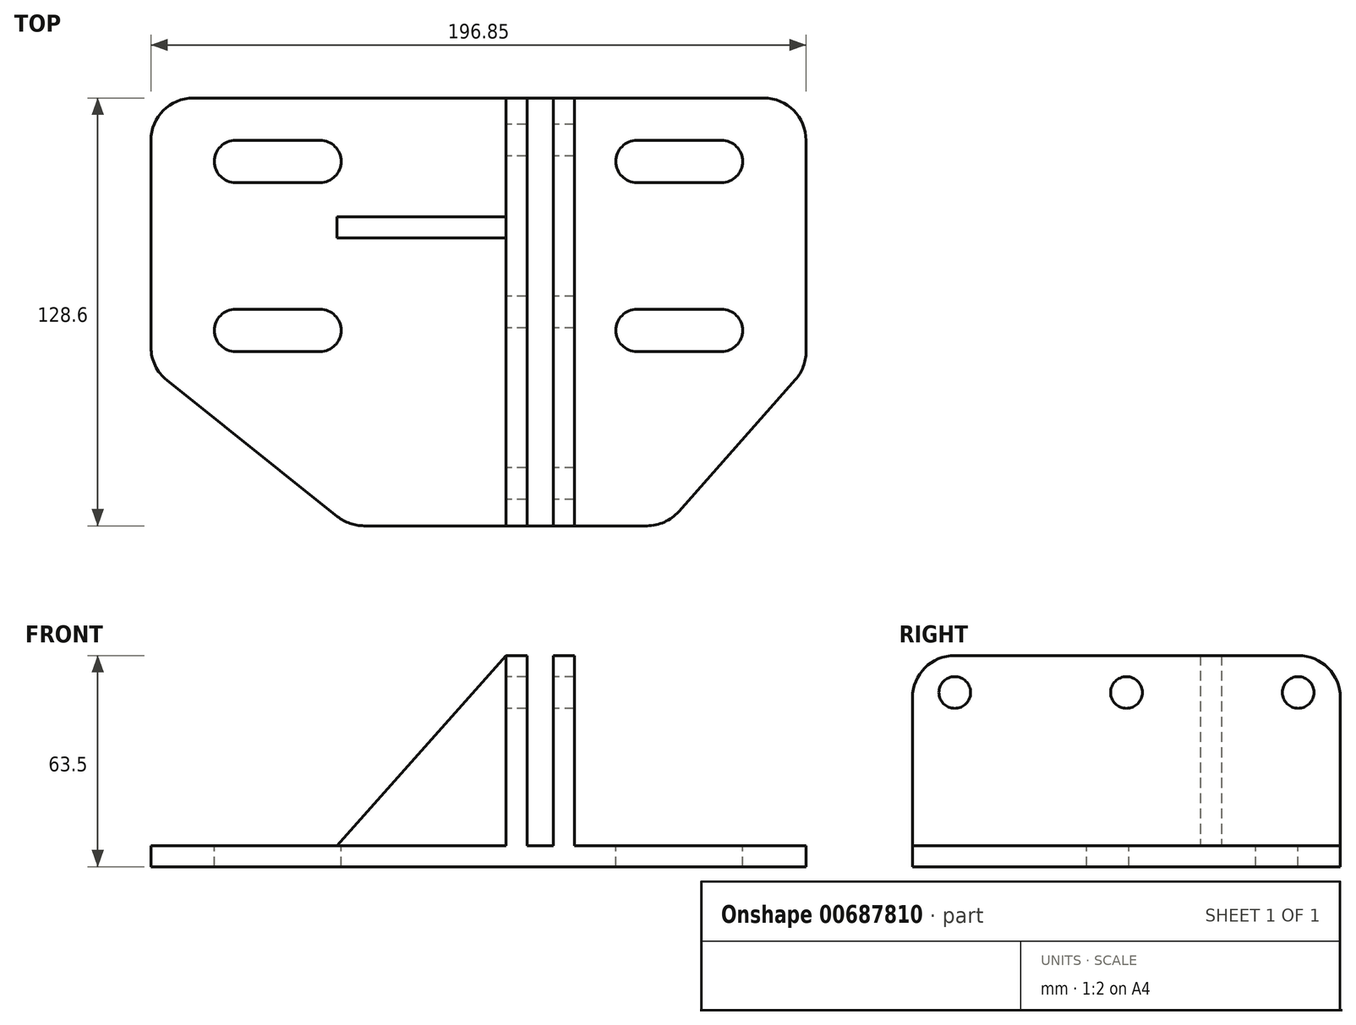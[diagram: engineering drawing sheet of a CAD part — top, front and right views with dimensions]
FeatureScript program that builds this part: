
annotation { "Feature Type Name" : "Feature", "Feature Type Description" : "" }
export const myFeature = defineFeature(function(context is Context, id is Id, definition is map)
    precondition{}
    {
        {
            var Q0;
            Q0=qCreatedBy(makeId("Top.planeOp"),FACE);
            var sketch = newSketch(context, id + "F0", { "sketchPlane" : qUnion([Q0])});
            skLineSegment(sketch, "E0", {"start": v(-88.28, 54.8) * mm, "end": v(83.17, 54.8) * mm});
            skLineSegment(sketch, "E1", {"start": v(95.87, 42.1) * mm, "end": v(95.87, -21.42) * mm});
            skLineSegment(sketch, "E2", {"start": v(92.69, -29.84) * mm, "end": v(57.6, -69.51) * mm});
            skLineSegment(sketch, "E3", {"start": v(48.08, -73.8) * mm, "end": v(-37, -73.8) * mm});
            skLineSegment(sketch, "E4", {"start": v(-44.92, -71.02) * mm, "end": v(-96.2, -30.05) * mm});
            skLineSegment(sketch, "E5", {"start": v(-100.98, -20.13) * mm, "end": v(-100.98, 42.1) * mm});
            skPoint(sketch, "E6.visualSharp", {"position": v(-100.98, 54.8) * mm});
            skArc(sketch, "E6.filletArc", {"start": v(-88.28, 54.8) * mm, "mid": v(-97.26, 51.08) * mm, "end": v(-100.98, 42.1) * mm});
            skPoint(sketch, "E7.visualSharp", {"position": v(95.87, 54.8) * mm});
            skArc(sketch, "E7.filletArc", {"start": v(95.87, 42.1) * mm, "mid": v(92.15, 51.08) * mm, "end": v(83.17, 54.8) * mm});
            skPoint(sketch, "E8.visualSharp", {"position": v(-41.45, -73.8) * mm});
            skArc(sketch, "E8.filletArc", {"start": v(-44.92, -71.02) * mm, "mid": v(-41.2, -73.09) * mm, "end": v(-37, -73.8) * mm});
            skPoint(sketch, "E9.visualSharp", {"position": v(53.8, -73.8) * mm});
            skArc(sketch, "E9.filletArc", {"start": v(48.08, -73.8) * mm, "mid": v(53.3, -72.68) * mm, "end": v(57.6, -69.51) * mm});
            skPoint(sketch, "E10.visualSharp", {"position": v(-100.98, -26.23) * mm});
            skArc(sketch, "E10.filletArc", {"start": v(-100.98, -20.13) * mm, "mid": v(-99.72, -25.63) * mm, "end": v(-96.2, -30.05) * mm});
            skPoint(sketch, "E11.visualSharp", {"position": v(95.87, -26.23) * mm});
            skArc(sketch, "E11.filletArc", {"start": v(92.69, -29.84) * mm, "mid": v(95.05, -25.92) * mm, "end": v(95.87, -21.42) * mm});
            skSolve(sketch);
        }
        {
            var Q0;
            Q0=makeQuery(id+"F0.imprint","IMPRINT",FACE,{"disambiguationData":[TD([[makeQuery(id+"F0.imprint","IMPRINT",EDGE,{"derivedFrom":sQuery(id+"F0.wireOp",EDGE,"E0")}),-1.0]])]});
            extrude(context, id + "F1", {"entities" : qUnion([Q0]), "depth" : 6.35 * mm, "offsetDistance" : 25.4 * mm});
        }
        {
            var Q0;
            Q0=makeQuery(id+"F1.opExtrude","CAP_FACE",FACE,{"disambiguationData":[OSD([sQuery(id+"F0.wireOp",EDGE,"E0"),sQuery(id+"F0.wireOp",EDGE,"E1"),sQuery(id+"F0.wireOp",EDGE,"E2"),sQuery(id+"F0.wireOp",EDGE,"E3"),sQuery(id+"F0.wireOp",EDGE,"E4"),sQuery(id+"F0.wireOp",EDGE,"E5"),sQuery(id+"F0.wireOp",EDGE,"E6.filletArc"),sQuery(id+"F0.wireOp",EDGE,"E7.filletArc"),sQuery(id+"F0.wireOp",EDGE,"E8.filletArc"),sQuery(id+"F0.wireOp",EDGE,"E9.filletArc"),sQuery(id+"F0.wireOp",EDGE,"E10.filletArc"),sQuery(id+"F0.wireOp",EDGE,"E11.filletArc")])],"isStart":false});
            var sketch = newSketch(context, id + "F2", { "sketchPlane" : qUnion([Q0])});
            skLineSegment(sketch, "E12.bottom", {"start": v(-50.18, -8.7) * mm, "end": v(-75.58, -8.7) * mm});
            skLineSegment(sketch, "E12.top", {"start": v(-50.18, -21.4) * mm, "end": v(-75.58, -21.4) * mm});
            skLineSegment(sketch, "E12.left", {"start": v(-43.83, -15.05) * mm, "end": v(-43.83, -15.05) * mm});
            skLineSegment(sketch, "E12.right", {"start": v(-81.93, -15.05) * mm, "end": v(-81.93, -15.05) * mm});
            skPoint(sketch, "E12.middle", {"position": v(-62.88, -15.05) * mm});
            skLineSegment(sketch, "E13.bottom", {"start": v(70.47, -8.7) * mm, "end": v(45.07, -8.7) * mm});
            skLineSegment(sketch, "E13.top", {"start": v(70.47, -21.4) * mm, "end": v(45.07, -21.4) * mm});
            skLineSegment(sketch, "E13.left", {"start": v(76.82, -15.05) * mm, "end": v(76.82, -15.05) * mm});
            skLineSegment(sketch, "E13.right", {"start": v(38.72, -15.05) * mm, "end": v(38.72, -15.05) * mm});
            skPoint(sketch, "E13.middle", {"position": v(57.77, -15.05) * mm});
            skLineSegment(sketch, "E14.bottom", {"start": v(45.07, 42.1) * mm, "end": v(70.47, 42.1) * mm});
            skLineSegment(sketch, "E14.top", {"start": v(45.07, 29.4) * mm, "end": v(70.47, 29.4) * mm});
            skLineSegment(sketch, "E14.left", {"start": v(38.72, 35.75) * mm, "end": v(38.72, 35.75) * mm});
            skLineSegment(sketch, "E14.right", {"start": v(76.82, 35.75) * mm, "end": v(76.82, 35.75) * mm});
            skPoint(sketch, "E14.middle", {"position": v(57.77, 35.75) * mm});
            skLineSegment(sketch, "E15.bottom", {"start": v(-75.58, 42.1) * mm, "end": v(-50.18, 42.1) * mm});
            skLineSegment(sketch, "E15.top", {"start": v(-75.58, 29.4) * mm, "end": v(-50.18, 29.4) * mm});
            skLineSegment(sketch, "E15.left", {"start": v(-81.93, 35.75) * mm, "end": v(-81.93, 35.75) * mm});
            skLineSegment(sketch, "E15.right", {"start": v(-43.83, 35.75) * mm, "end": v(-43.83, 35.75) * mm});
            skPoint(sketch, "E15.middle", {"position": v(-62.88, 35.75) * mm});
            skPoint(sketch, "E16.visualSharp", {"position": v(-81.93, -21.4) * mm});
            skArc(sketch, "E16.filletArc", {"start": v(-81.93, -15.05) * mm, "mid": v(-80.07, -19.54) * mm, "end": v(-75.58, -21.4) * mm});
            skPoint(sketch, "E17.visualSharp", {"position": v(-81.93, -8.7) * mm});
            skArc(sketch, "E17.filletArc", {"start": v(-75.58, -8.7) * mm, "mid": v(-80.07, -10.56) * mm, "end": v(-81.93, -15.05) * mm});
            skPoint(sketch, "E18.visualSharp", {"position": v(-43.83, -21.4) * mm});
            skArc(sketch, "E18.filletArc", {"start": v(-50.18, -21.4) * mm, "mid": v(-45.69, -19.54) * mm, "end": v(-43.83, -15.05) * mm});
            skPoint(sketch, "E19.visualSharp", {"position": v(-43.83, -8.7) * mm});
            skArc(sketch, "E19.filletArc", {"start": v(-43.83, -15.05) * mm, "mid": v(-45.69, -10.56) * mm, "end": v(-50.18, -8.7) * mm});
            skPoint(sketch, "E20.visualSharp", {"position": v(-43.83, 29.4) * mm});
            skArc(sketch, "E20.filletArc", {"start": v(-50.18, 29.4) * mm, "mid": v(-45.69, 31.26) * mm, "end": v(-43.83, 35.75) * mm});
            skPoint(sketch, "E21.visualSharp", {"position": v(-43.83, 42.1) * mm});
            skArc(sketch, "E21.filletArc", {"start": v(-43.83, 35.75) * mm, "mid": v(-45.69, 40.24) * mm, "end": v(-50.18, 42.1) * mm});
            skPoint(sketch, "E22.visualSharp", {"position": v(-81.93, 42.1) * mm});
            skArc(sketch, "E22.filletArc", {"start": v(-75.58, 42.1) * mm, "mid": v(-80.07, 40.24) * mm, "end": v(-81.93, 35.75) * mm});
            skPoint(sketch, "E23.visualSharp", {"position": v(-81.93, 29.4) * mm});
            skArc(sketch, "E23.filletArc", {"start": v(-81.93, 35.75) * mm, "mid": v(-80.07, 31.26) * mm, "end": v(-75.58, 29.4) * mm});
            skPoint(sketch, "E24.visualSharp", {"position": v(38.72, -21.4) * mm});
            skArc(sketch, "E24.filletArc", {"start": v(38.72, -15.05) * mm, "mid": v(40.58, -19.54) * mm, "end": v(45.07, -21.4) * mm});
            skPoint(sketch, "E25.visualSharp", {"position": v(38.72, -8.7) * mm});
            skArc(sketch, "E25.filletArc", {"start": v(45.07, -8.7) * mm, "mid": v(40.58, -10.56) * mm, "end": v(38.72, -15.05) * mm});
            skPoint(sketch, "E26.visualSharp", {"position": v(76.82, -21.4) * mm});
            skArc(sketch, "E26.filletArc", {"start": v(70.47, -21.4) * mm, "mid": v(74.96, -19.54) * mm, "end": v(76.82, -15.05) * mm});
            skPoint(sketch, "E27.visualSharp", {"position": v(76.82, -8.7) * mm});
            skArc(sketch, "E27.filletArc", {"start": v(76.82, -15.05) * mm, "mid": v(74.96, -10.56) * mm, "end": v(70.47, -8.7) * mm});
            skPoint(sketch, "E28.visualSharp", {"position": v(76.82, 29.4) * mm});
            skArc(sketch, "E28.filletArc", {"start": v(70.47, 29.4) * mm, "mid": v(74.96, 31.26) * mm, "end": v(76.82, 35.75) * mm});
            skPoint(sketch, "E29.visualSharp", {"position": v(76.82, 42.1) * mm});
            skArc(sketch, "E29.filletArc", {"start": v(76.82, 35.75) * mm, "mid": v(74.96, 40.24) * mm, "end": v(70.47, 42.1) * mm});
            skPoint(sketch, "E30.visualSharp", {"position": v(38.72, 42.1) * mm});
            skArc(sketch, "E30.filletArc", {"start": v(45.07, 42.1) * mm, "mid": v(40.58, 40.24) * mm, "end": v(38.72, 35.75) * mm});
            skPoint(sketch, "E31.visualSharp", {"position": v(38.72, 29.4) * mm});
            skArc(sketch, "E31.filletArc", {"start": v(38.72, 35.75) * mm, "mid": v(40.58, 31.26) * mm, "end": v(45.07, 29.4) * mm});
            skSolve(sketch);
        }
        {
            var Q0;
            Q0 = qSketchRegion(id + "F2", true);
            extrude(context, id + "F3", {"entities" : qUnion([Q0]), "operationType" : NewBodyOperationType.REMOVE, "endBound" : BoundingType.THROUGH_ALL, "oppositeDirection" : true, "depth" : 25.4 * mm, "offsetDistance" : 25.4 * mm});
        }
        {
            var Q0;
            Q0=makeQuery(id+"F1.opExtrude","CAP_FACE",FACE,{"disambiguationData":[OSD([sQuery(id+"F0.wireOp",EDGE,"E0"),sQuery(id+"F0.wireOp",EDGE,"E1"),sQuery(id+"F0.wireOp",EDGE,"E2"),sQuery(id+"F0.wireOp",EDGE,"E3"),sQuery(id+"F0.wireOp",EDGE,"E4"),sQuery(id+"F0.wireOp",EDGE,"E5"),sQuery(id+"F0.wireOp",EDGE,"E6.filletArc"),sQuery(id+"F0.wireOp",EDGE,"E7.filletArc"),sQuery(id+"F0.wireOp",EDGE,"E8.filletArc"),sQuery(id+"F0.wireOp",EDGE,"E9.filletArc"),sQuery(id+"F0.wireOp",EDGE,"E10.filletArc"),sQuery(id+"F0.wireOp",EDGE,"E11.filletArc")])],"isStart":false});
            var sketch = newSketch(context, id + "F4", { "sketchPlane" : qUnion([Q0])});
            skLineSegment(sketch, "E32.bottom", {"start": v(5.7, 54.8) * mm, "end": v(12.04, 54.8) * mm});
            skLineSegment(sketch, "E32.top", {"start": v(5.7, -73.8) * mm, "end": v(12.04, -73.8) * mm});
            skLineSegment(sketch, "E32.left", {"start": v(5.7, 54.8) * mm, "end": v(5.7, -73.8) * mm});
            skLineSegment(sketch, "E32.right", {"start": v(12.04, 54.8) * mm, "end": v(12.04, -73.8) * mm});
            skLineSegment(sketch, "E33.bottom", {"start": v(26.33, 54.8) * mm, "end": v(19.98, 54.8) * mm});
            skLineSegment(sketch, "E33.top", {"start": v(26.33, -73.8) * mm, "end": v(19.98, -73.8) * mm});
            skLineSegment(sketch, "E33.left", {"start": v(26.33, 54.8) * mm, "end": v(26.33, -73.8) * mm});
            skLineSegment(sketch, "E33.right", {"start": v(19.98, 54.8) * mm, "end": v(19.98, -73.8) * mm});
            skSolve(sketch);
        }
        {
            var Q0;
            Q0 = qSketchRegion(id + "F4", true);
            extrude(context, id + "F5", {"entities" : qUnion([Q0]), "operationType" : NewBodyOperationType.ADD, "depth" : 57.15 * mm, "offsetDistance" : 25.4 * mm});
        }
        {
            var Q0;
            Q0=makeQuery(id+"F5.opExtrude","SWEPT_FACE",FACE,{"disambiguationData":[OSD([sQuery(id+"F4.wireOp",EDGE,"E32.left")])]});
            var sketch = newSketch(context, id + "F6", { "sketchPlane" : qUnion([Q0])});
            skCircle(sketch, "E34", {"center": v(-42.1, 52.39) * mm, "radius": 4.76 * mm});
            skCircle(sketch, "E35", {"center": v(9.5, 52.39) * mm, "radius": 4.76 * mm});
            skCircle(sketch, "E36", {"center": v(61.1, 52.39) * mm, "radius": 4.76 * mm});
            skSolve(sketch);
        }
        {
            var Q0;
            Q0=makeQuery(id+"F6.imprint","IMPRINT",FACE,{"disambiguationData":[TD([[makeQuery(id+"F6.imprint","IMPRINT",EDGE,{"derivedFrom":sQuery(id+"F6.wireOp",EDGE,"E34")}),1.0]])]});
            var Q1;
            Q1=makeQuery(id+"F6.imprint","IMPRINT",FACE,{"disambiguationData":[TD([[makeQuery(id+"F6.imprint","IMPRINT",EDGE,{"derivedFrom":sQuery(id+"F6.wireOp",EDGE,"E35")}),1.0]])]});
            var Q2;
            Q2=makeQuery(id+"F6.imprint","IMPRINT",FACE,{"disambiguationData":[TD([[makeQuery(id+"F6.imprint","IMPRINT",EDGE,{"derivedFrom":sQuery(id+"F6.wireOp",EDGE,"E36")}),1.0]])]});
            extrude(context, id + "F7", {"entities" : qUnion([Q0, Q1, Q2]), "operationType" : NewBodyOperationType.REMOVE, "endBound" : BoundingType.THROUGH_ALL, "oppositeDirection" : true, "depth" : 25.4 * mm, "offsetDistance" : 25.4 * mm});
        }
        {
            var Q0;
            Q0=qCreatedBy(makeId("Front.planeOp"),FACE);
            cPlane(context, id + "F8", {"entities" : qUnion([Q0]), "cplaneType" : CPlaneType.OFFSET, "offset" : 12.7 * mm, "oppositeDirection" : true, "width" : 152.4 * mm, "height" : 152.4 * mm});
        }
        {
            var Q0;
            Q0=qCreatedBy(id+"F8.planeOp",FACE);
            var sketch = newSketch(context, id + "F9", { "sketchPlane" : qUnion([Q0])});
            skLineSegment(sketch, "E37", {"start": v(5.7, 63.5) * mm, "end": v(5.7, 6.35) * mm});
            skLineSegment(sketch, "E38", {"start": v(5.7, 6.35) * mm, "end": v(-45.1, 6.35) * mm});
            skLineSegment(sketch, "E39", {"start": v(-45.1, 6.35) * mm, "end": v(5.7, 63.5) * mm});
            skSolve(sketch);
        }
        {
            var Q0;
            Q0 = qSketchRegion(id + "F9", true);
            extrude(context, id + "F10", {"entities" : qUnion([Q0]), "operationType" : NewBodyOperationType.ADD, "oppositeDirection" : true, "depth" : 6.35 * mm, "offsetDistance" : 25.4 * mm});
        }
        {
            var Q0;
            Q0=makeQuery(id+"F5.opExtrude","CAP_EDGE",EDGE,{"disambiguationData":[OSD([sQuery(id+"F4.wireOp",EDGE,"E32.top")])],"isStart":false});
            var Q1;
            Q1=makeQuery(id+"F5.opExtrude","CAP_EDGE",EDGE,{"disambiguationData":[OSD([sQuery(id+"F4.wireOp",EDGE,"E33.top")])],"isStart":false});
            var Q2;
            Q2=makeQuery(id+"F5.opExtrude","CAP_EDGE",EDGE,{"disambiguationData":[OSD([sQuery(id+"F4.wireOp",EDGE,"E33.bottom")])],"isStart":false});
            var Q3;
            Q3=makeQuery(id+"F5.opExtrude","CAP_EDGE",EDGE,{"disambiguationData":[OSD([sQuery(id+"F4.wireOp",EDGE,"E32.bottom")])],"isStart":false});
            fillet(context, id + "F11", {"entities" : qUnion([Q0, Q1, Q2, Q3]), "radius" : 12.7 * mm, "tangentPropagation" : true, "allowEdgeOverflow" : false});
        }
    });
